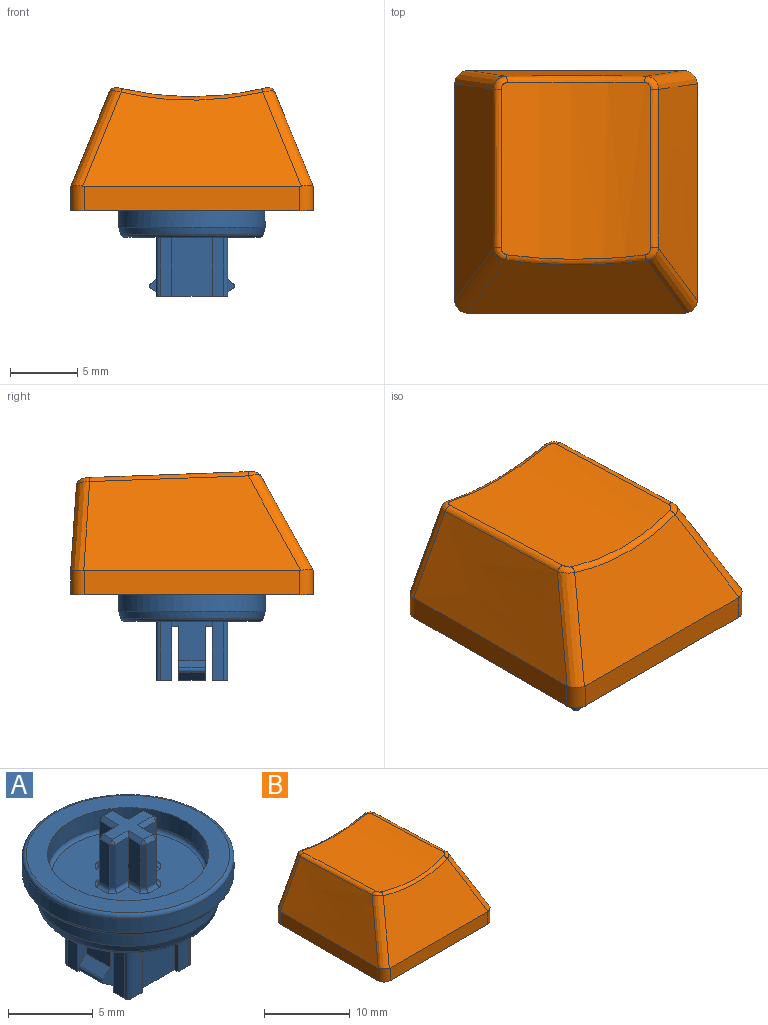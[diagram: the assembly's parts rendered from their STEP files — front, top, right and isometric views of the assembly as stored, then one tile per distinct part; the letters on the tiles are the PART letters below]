
ASSEMBLY  parts=2 mates=1
PART A: 171 faces, bbox 13.5x13.5x10 mm
  f0: cylinder r=4.2mm len=8.4mm, axis (0,0,-1), area 2.6mm2, adj f169,f170
  f1: plane 10.05x10.05mm, normal (0,0,-1), area 17.1mm2, adj f4,f170
  f2: cone r=5.25mm half-angle=15.9deg, axis (0,0,1), area 17mm2, adj f3,f4
  f3: cylinder r=5.45mm len=10.9mm, axis (0,0,-1), area 44.5mm2, adj f2,f79
  f4: torus R=5.02mm, axis (0,0,1), area 12.6mm2, adj f1,f2
  f5: plane 0.9x0.9mm, normal (0,0,-1), area 0.6mm2, adj f14
  f6: plane 0.5x0.2mm, normal (0,-0.71,-0.71), area 0.1mm2, adj f11,f15,f16,f17
  f7: plane 0.5x0.2mm, normal (-0.71,0,-0.71), area 0.1mm2, adj f10,f18,f19,f20
  f8: plane 0.5x0.2mm, normal (0,0.71,-0.71), area 0.1mm2, adj f13,f21,f22,f23
  f9: plane 0.5x0.2mm, normal (0.71,0,-0.71), area 0.1mm2, adj f12,f24,f25,f26
  f10: plane 0.5x0.09mm, normal (0,0,-1), area 0mm2, adj f7,f18,f20,f27
  f11: plane 0.5x0.09mm, normal (0,0,-1), area 0mm2, adj f6,f15,f17,f27
  f12: plane 0.5x0.09mm, normal (0,0,-1), area 0mm2, adj f9,f24,f26,f27
  f13: plane 0.5x0.09mm, normal (0,0,-1), area 0mm2, adj f8,f21,f23,f27
  f14: torus R=0.45mm, axis (0,0,-1), area 1.9mm2, adj f5,f27
  f15: plane 2.5x0.29mm, normal (1,0,0), area 0.7mm2, adj f6,f11,f16,f27,f34
  f16: plane 2.3x0.5mm, normal (0,-1,0), area 1.1mm2, adj f6,f15,f17,f34
  f17: plane 2.5x0.29mm, normal (-1,0,0), area 0.7mm2, adj f6,f11,f16,f27,f34
  f18: plane 2.5x0.29mm, normal (0,-1,0), area 0.7mm2, adj f7,f10,f19,f27,f34
  f19: plane 2.3x0.5mm, normal (-1,0,0), area 1.1mm2, adj f7,f18,f20,f34
  f20: plane 2.5x0.29mm, normal (0,1,0), area 0.7mm2, adj f7,f10,f19,f27,f34
  f21: plane 2.5x0.29mm, normal (-1,0,0), area 0.7mm2, adj f8,f13,f22,f27,f34
  f22: plane 2.3x0.5mm, normal (0,1,0), area 1.1mm2, adj f8,f21,f23,f34
  f23: plane 2.5x0.29mm, normal (1,0,0), area 0.7mm2, adj f8,f13,f22,f27,f34
  f24: plane 2.5x0.29mm, normal (0,1,0), area 0.7mm2, adj f9,f12,f25,f27,f34
  f25: plane 2.3x0.5mm, normal (1,0,0), area 1.1mm2, adj f9,f24,f26,f34
  f26: plane 2.5x0.29mm, normal (0,-1,0), area 0.7mm2, adj f9,f12,f25,f27,f34
  f27: cylinder r=0.75mm len=2.7mm, axis (0,0,1), area 7.6mm2, adj f10,f11,f12,f13,f14,f15,f17,f18
  f28: plane 2x0.91mm, normal (0.55,0,-0.83), area 2.2mm2, adj f29,f33,f35,f37
  f29: cylinder r=0.2mm len=2mm, axis (0,1,0), area 0.7mm2, adj f28,f35,f37,f38
  f30: plane 2x0.91mm, normal (-0.55,0,-0.83), area 2.2mm2, adj f31,f32,f40,f41
  f31: cylinder r=0.2mm len=2mm, axis (0,1,0), area 0.7mm2, adj f30,f40,f41,f42
  f32: plane 2x0.3mm, normal (0,0,-1), area 0.6mm2, adj f30,f40,f41,f46
  f33: plane 2x0.3mm, normal (0,0,-1), area 0.6mm2, adj f28,f35,f37,f48
  f34: plane 3.75x3.75mm, normal (0,0,-1), area 11.8mm2, adj f15,f16,f17,f18,f19,f20,f21,f22
  f35: plane 4x1.3mm, normal (0,-1,0), area 2.9mm2, adj f28,f29,f33,f38,f39,f48,f50
  f36: plane 0.6x0.5mm, normal (0,0,-1), area 0.3mm2, adj f37,f48,f49,f50
  f37: plane 4x1.3mm, normal (0,1,0), area 2.9mm2, adj f28,f29,f33,f36,f38,f48,f50
  f38: plane 2x0.63mm, normal (0.64,0,0.77), area 1.6mm2, adj f29,f35,f37,f50
  f39: plane 0.6x0.5mm, normal (0,0,-1), area 0.3mm2, adj f35,f48,f50,f51
  f40: plane 4x1.3mm, normal (0,1,0), area 2.9mm2, adj f30,f31,f32,f42,f43,f46,f59
  f41: plane 4x1.3mm, normal (0,-1,0), area 2.9mm2, adj f30,f31,f32,f42,f44,f46,f59
  f42: plane 2x0.63mm, normal (-0.64,0,0.77), area 1.6mm2, adj f31,f40,f41,f59
  f43: plane 0.6x0.5mm, normal (0,0,-1), area 0.3mm2, adj f40,f46,f59,f67
  f44: plane 0.6x0.5mm, normal (0,0,-1), area 0.3mm2, adj f41,f46,f59,f68
  f45: plane 5x3.75mm, normal (0,1,0), area 18.8mm2, adj f34,f46,f48,f72
  f46: plane 5x3.75mm, normal (1,0,0), area 14.8mm2, adj f32,f34,f40,f41,f43,f44,f45,f47
  f47: plane 5x3.75mm, normal (0,-1,0), area 18.8mm2, adj f34,f46,f48,f63
  f48: plane 5x3.75mm, normal (-1,0,0), area 14.8mm2, adj f33,f34,f35,f36,f37,f39,f45,f47
  f49: plane 4.75x0.8mm, normal (0,-1,0), area 3.3mm2, adj f36,f48,f50,f63,f66,f147
  f50: plane 3.3x3mm, normal (1,0,0), area 7.4mm2, adj f35,f36,f37,f38,f39,f49,f51,f149
  f51: plane 4.75x0.8mm, normal (0,1,0), area 3.3mm2, adj f39,f48,f50,f71,f72,f151
  f52: plane 4.75x3mm, normal (0,1,0), area 14.2mm2, adj f53,f54,f63,f152
  f53: plane 4.75x0.3mm, normal (1,0,0), area 1.4mm2, adj f52,f62,f63,f154
  f54: plane 4.75x0.3mm, normal (-1,0,0), area 1.4mm2, adj f52,f63,f65,f150
  f55: plane 4.75x3mm, normal (0,-1,0), area 14.2mm2, adj f56,f58,f72,f161
  f56: plane 4.75x0.3mm, normal (1,0,0), area 1.4mm2, adj f55,f72,f75,f163
  f57: plane 7.9x7.9mm, normal (0,0,-1), area 17.6mm2, adj f145,f146,f147,f148,f149,f150,f151,f152
  f58: plane 4.75x0.3mm, normal (-1,0,0), area 1.4mm2, adj f55,f70,f72,f159
  f59: plane 3.3x3mm, normal (-1,0,0), area 7.4mm2, adj f40,f41,f42,f43,f44,f67,f68,f164
  f60: cylinder r=0.3mm len=4.75mm, axis (0,0,-1), area 2.2mm2, adj f61,f62,f63,f158
  f61: plane 4.75x0.88mm, normal (-1,0,0), area 4.2mm2, adj f60,f63,f67,f160
  f62: plane 4.75x0.88mm, normal (0,1,0), area 4.2mm2, adj f53,f60,f63,f156
  f63: plane 5.35x1.18mm, normal (0,0,-1), area 3.9mm2, adj f46,f47,f48,f49,f52,f53,f54,f60
  f64: cylinder r=0.3mm len=4.75mm, axis (0,0,1), area 2.2mm2, adj f63,f65,f66,f146
  f65: plane 4.75x0.88mm, normal (0,1,0), area 4.2mm2, adj f54,f63,f64,f148
  f66: plane 4.75x0.88mm, normal (1,0,0), area 4.2mm2, adj f49,f63,f64,f145
  f67: plane 4.75x0.8mm, normal (0,-1,0), area 3.4mm2, adj f43,f46,f59,f61,f63,f162
  f68: plane 4.75x0.8mm, normal (0,1,0), area 3.4mm2, adj f44,f46,f59,f72,f74,f166
  f69: cylinder r=0.3mm len=4.75mm, axis (0,0,-1), area 2.2mm2, adj f70,f71,f72,f155
  f70: plane 4.75x0.88mm, normal (0,-1,0), area 4.2mm2, adj f58,f69,f72,f157
  f71: plane 4.75x0.88mm, normal (1,0,0), area 4.2mm2, adj f51,f69,f72,f153
  f72: plane 5.35x1.18mm, normal (0,0,-1), area 3.9mm2, adj f45,f46,f48,f51,f55,f56,f58,f68
  f73: cylinder r=0.3mm len=4.75mm, axis (0,0,1), area 2.2mm2, adj f72,f74,f75,f167
  f74: plane 4.75x0.88mm, normal (-1,0,0), area 4.2mm2, adj f68,f72,f73,f168
  f75: plane 4.75x0.88mm, normal (0,-1,0), area 4.2mm2, adj f56,f72,f73,f165
  f76: cylinder r=6.25mm len=12.5mm, axis (0,0,-1), area 39.3mm2, adj f143,f144
  f77: cylinder r=4.75mm len=9.5mm, axis (0,0,-1), area 37.3mm2, adj f78,f142
  f78: plane 12x12mm, normal (0,0,1), area 42.2mm2, adj f77,f144
  f79: plane 12x12mm, normal (0,0,-1), area 19.8mm2, adj f3,f143
  f80: plane 9x9mm, normal (0,0,1), area 51.8mm2, adj f122,f123,f124,f125,f126,f127,f128,f129
  f81: plane 3.1x1.06mm, normal (1,0,0), area 3.3mm2, adj f92,f118,f121,f127
  f82: plane 3.1x0.78mm, normal (0,1,0), area 2.4mm2, adj f115,f119,f121,f123
  f83: plane 3.1x1.06mm, normal (-1,0,0), area 3.3mm2, adj f84,f114,f115,f124
  f84: plane 3.1x1.06mm, normal (0,1,0), area 3.3mm2, adj f83,f107,f112,f126
  f85: plane 3.1x0.78mm, normal (-1,0,0), area 2.4mm2, adj f101,f106,f107,f130
  f86: plane 3.1x1.06mm, normal (0,-1,0), area 3.3mm2, adj f87,f100,f101,f134
  f87: plane 3.1x1.06mm, normal (-1,0,0), area 3.3mm2, adj f86,f94,f98,f136
  f88: plane 3.1x0.78mm, normal (0,-1,0), area 2.4mm2, adj f94,f96,f97,f140
  f89: plane 3.1x1.06mm, normal (1,0,0), area 3.3mm2, adj f90,f96,f102,f139
  f90: plane 3.1x1.06mm, normal (0,-1,0), area 3.3mm2, adj f89,f104,f105,f137
  f91: plane 3.1x0.78mm, normal (1,0,0), area 2.4mm2, adj f104,f110,f111,f133
  f92: plane 3.1x1.06mm, normal (0,1,0), area 3.3mm2, adj f81,f110,f116,f129
  f93: plane 3.4x3.4mm, normal (0,0,1), area 4.7mm2, adj f97,f98,f100,f102,f105,f106,f111,f112
  f94: plane 3.1x0.25mm, normal (-0.71,-0.71,0), area 1.1mm2, adj f87,f88,f95,f138
  f95: plane 0.25x0.25mm, normal (-0.58,-0.58,0.58), area 0.1mm2, adj f94,f97,f98
  f96: plane 3.1x0.25mm, normal (0.71,-0.71,0), area 1.1mm2, adj f88,f89,f99,f141
  f97: plane 0.78x0.25mm, normal (0,-0.71,0.71), area 0.3mm2, adj f88,f93,f95,f99
  f98: plane 1.31x0.25mm, normal (-0.71,0,0.71), area 0.4mm2, adj f87,f93,f95,f100
  f99: plane 0.25x0.25mm, normal (0.58,-0.58,0.58), area 0.1mm2, adj f96,f97,f102
  f100: plane 1.31x0.25mm, normal (0,-0.71,0.71), area 0.4mm2, adj f86,f93,f98,f103
  f101: plane 3.1x0.25mm, normal (-0.71,-0.71,0), area 1.1mm2, adj f85,f86,f103,f132
  f102: plane 1.31x0.25mm, normal (0.71,0,0.71), area 0.4mm2, adj f89,f93,f99,f105
  f103: plane 0.25x0.25mm, normal (-0.58,-0.58,0.58), area 0.1mm2, adj f100,f101,f106
  f104: plane 3.1x0.25mm, normal (0.71,-0.71,0), area 1.1mm2, adj f90,f91,f108,f135
  f105: plane 1.31x0.25mm, normal (0,-0.71,0.71), area 0.4mm2, adj f90,f93,f102,f108
  f106: plane 0.78x0.25mm, normal (-0.71,0,0.71), area 0.3mm2, adj f85,f93,f103,f109
  f107: plane 3.1x0.25mm, normal (-0.71,0.71,0), area 1.1mm2, adj f84,f85,f109,f128
  f108: plane 0.25x0.25mm, normal (0.58,-0.58,0.58), area 0.1mm2, adj f104,f105,f111
  f109: plane 0.25x0.25mm, normal (-0.58,0.58,0.58), area 0.1mm2, adj f106,f107,f112
  f110: plane 3.1x0.25mm, normal (0.71,0.71,0), area 1.1mm2, adj f91,f92,f113,f131
  f111: plane 0.78x0.25mm, normal (0.71,0,0.71), area 0.3mm2, adj f91,f93,f108,f113
  f112: plane 1.31x0.25mm, normal (0,0.71,0.71), area 0.4mm2, adj f84,f93,f109,f114
  f113: plane 0.25x0.25mm, normal (0.58,0.58,0.58), area 0.1mm2, adj f110,f111,f116
  f114: plane 1.31x0.25mm, normal (-0.71,0,0.71), area 0.4mm2, adj f83,f93,f112,f117
  f115: plane 3.1x0.25mm, normal (-0.71,0.71,0), area 1.1mm2, adj f82,f83,f117,f122
  f116: plane 1.31x0.25mm, normal (0,0.71,0.71), area 0.4mm2, adj f92,f93,f113,f118
  f117: plane 0.25x0.25mm, normal (-0.58,0.58,0.58), area 0.1mm2, adj f114,f115,f119
  f118: plane 1.31x0.25mm, normal (0.71,0,0.71), area 0.4mm2, adj f81,f93,f116,f120
  f119: plane 0.78x0.25mm, normal (0,0.71,0.71), area 0.3mm2, adj f82,f93,f117,f120
  f120: plane 0.25x0.25mm, normal (0.58,0.58,0.58), area 0.1mm2, adj f118,f119,f121
  f121: plane 3.1x0.25mm, normal (0.71,0.71,0), area 1.1mm2, adj f81,f82,f120,f125
  f122: cylinder r=0.25mm len=0.57mm, axis (0.71,0.71,0), area 0.2mm2, adj f80,f115,f123,f124
  f123: cylinder r=0.25mm len=0.99mm, axis (-1,0,0), area 0.3mm2, adj f80,f82,f122,f125
  f124: cylinder r=0.25mm len=1.16mm, axis (0,-1,0), area 0.4mm2, adj f80,f83,f122,f126
  f125: cylinder r=0.25mm len=0.57mm, axis (-0.71,0.71,0), area 0.2mm2, adj f80,f121,f123,f127
  f126: cylinder r=0.25mm len=1.16mm, axis (-1,0,0), area 0.4mm2, adj f80,f84,f124,f128
  f127: cylinder r=0.25mm len=1.16mm, axis (0,1,0), area 0.4mm2, adj f80,f81,f125,f129
  f128: cylinder r=0.25mm len=0.57mm, axis (0.71,0.71,0), area 0.2mm2, adj f80,f107,f126,f130
  f129: cylinder r=0.25mm len=1.16mm, axis (-1,0,0), area 0.4mm2, adj f80,f92,f127,f131
  f130: cylinder r=0.25mm len=0.99mm, axis (0,-1,0), area 0.3mm2, adj f80,f85,f128,f132
  f131: cylinder r=0.25mm len=0.57mm, axis (-0.71,0.71,0), area 0.2mm2, adj f80,f110,f129,f133
  f132: cylinder r=0.25mm len=0.57mm, axis (0.71,-0.71,0), area 0.2mm2, adj f80,f101,f130,f134
  f133: cylinder r=0.25mm len=0.99mm, axis (0,1,0), area 0.3mm2, adj f80,f91,f131,f135
  f134: cylinder r=0.25mm len=1.16mm, axis (1,0,0), area 0.4mm2, adj f80,f86,f132,f136
  f135: cylinder r=0.25mm len=0.57mm, axis (-0.71,-0.71,0), area 0.2mm2, adj f80,f104,f133,f137
  f136: cylinder r=0.25mm len=1.16mm, axis (0,-1,0), area 0.4mm2, adj f80,f87,f134,f138
  f137: cylinder r=0.25mm len=1.16mm, axis (1,0,0), area 0.4mm2, adj f80,f90,f135,f139
  f138: cylinder r=0.25mm len=0.57mm, axis (0.71,-0.71,0), area 0.2mm2, adj f80,f94,f136,f140
  f139: cylinder r=0.25mm len=1.16mm, axis (0,1,0), area 0.4mm2, adj f80,f89,f137,f141
  f140: cylinder r=0.25mm len=0.99mm, axis (1,0,0), area 0.3mm2, adj f80,f88,f138,f141
  f141: cylinder r=0.25mm len=0.57mm, axis (-0.71,-0.71,0), area 0.2mm2, adj f80,f96,f139,f140
  f142: torus R=4.5mm, axis (0,0,1), area 11.5mm2, adj f77,f80
  f143: torus R=6mm, axis (0,0,1), area 15.2mm2, adj f76,f79
  f144: torus R=6mm, axis (0,0,1), area 15.2mm2, adj f76,f78
  f145: cylinder r=0.25mm len=1.13mm, axis (0,1,0), area 0.4mm2, adj f57,f66,f146,f147
  f146: torus R=0.55mm, axis (0,0,-1), area 0.2mm2, adj f57,f64,f145,f148
  f147: cylinder r=0.25mm len=0.45mm, axis (1,0,0), area 0.1mm2, adj f49,f57,f145,f149
  f148: cylinder r=0.25mm len=1.13mm, axis (-1,0,0), area 0.4mm2, adj f57,f65,f146,f150
  f149: cylinder r=0.25mm len=3mm, axis (0,1,0), area 1.1mm2, adj f50,f57,f147,f151
  f150: cylinder r=0.25mm len=0.55mm, axis (0,-1,0), area 0.1mm2, adj f54,f57,f148,f152
  f151: cylinder r=0.25mm len=0.45mm, axis (-1,0,0), area 0.1mm2, adj f51,f57,f149,f153
  f152: cylinder r=0.25mm len=3mm, axis (-1,0,0), area 1.1mm2, adj f52,f57,f150,f154
  f153: cylinder r=0.25mm len=1.13mm, axis (0,1,0), area 0.4mm2, adj f57,f71,f151,f155
  f154: cylinder r=0.25mm len=0.55mm, axis (0,1,0), area 0.1mm2, adj f53,f57,f152,f156
  f155: torus R=0.55mm, axis (0,0,-1), area 0.2mm2, adj f57,f69,f153,f157
  f156: cylinder r=0.25mm len=1.13mm, axis (-1,0,0), area 0.4mm2, adj f57,f62,f154,f158
  f157: cylinder r=0.25mm len=1.13mm, axis (1,0,0), area 0.4mm2, adj f57,f70,f155,f159
  f158: torus R=0.55mm, axis (0,0,-1), area 0.2mm2, adj f57,f60,f156,f160
  f159: cylinder r=0.25mm len=0.55mm, axis (0,-1,0), area 0.1mm2, adj f57,f58,f157,f161
  f160: cylinder r=0.25mm len=1.13mm, axis (0,-1,0), area 0.4mm2, adj f57,f61,f158,f162
  f161: cylinder r=0.25mm len=3mm, axis (1,0,0), area 1.1mm2, adj f55,f57,f159,f163
  f162: cylinder r=0.25mm len=0.45mm, axis (1,0,0), area 0.1mm2, adj f57,f67,f160,f164
  f163: cylinder r=0.25mm len=0.55mm, axis (0,1,0), area 0.1mm2, adj f56,f57,f161,f165
  f164: cylinder r=0.25mm len=3mm, axis (0,-1,0), area 1.1mm2, adj f57,f59,f162,f166
  f165: cylinder r=0.25mm len=1.13mm, axis (1,0,0), area 0.4mm2, adj f57,f75,f163,f167
  f166: cylinder r=0.25mm len=0.45mm, axis (-1,0,0), area 0.1mm2, adj f57,f68,f164,f168
  f167: torus R=0.55mm, axis (0,0,-1), area 0.2mm2, adj f57,f73,f165,f168
  f168: cylinder r=0.25mm len=1.13mm, axis (0,-1,0), area 0.4mm2, adj f57,f74,f166,f167
  f169: torus R=3.95mm, axis (0,0,-1), area 10.1mm2, adj f0,f57
  f170: torus R=4.45mm, axis (0,0,1), area 10.6mm2, adj f0,f1
PART B: 50 faces, bbox 21.6x22.4x13.2 mm
  f0: plane 18.1x18.1mm, normal (0,0,-1), area 67.5mm2, adj f1,f2,f3,f4,f10,f12,f14,f16
  f1: plane 16.1x1.8mm, normal (1,0,0), area 29mm2, adj f0,f8,f10,f16
  f2: plane 16.11x1.81mm, normal (0,1,0), area 29mm2, adj f0,f5,f14,f15,f16,f17
  f3: plane 16.1x1.8mm, normal (-1,0,0), area 29mm2, adj f0,f6,f12,f14
  f4: plane 16.1x1.8mm, normal (0,-1,0), area 29mm2, adj f0,f7,f10,f12
  f5: plane 15.98x6.33mm, normal (0,1,0.07), area 79.8mm2, adj f2,f15,f17,f20
  f6: bspline ~18.1x7.49mm, area 104.4mm2, adj f3,f12,f13,f14,f15,f19
  f7: plane 16.33x7.03mm, normal (0,-0.87,0.48), area 103.3mm2, adj f4,f10,f11,f12,f13,f23
  f8: bspline ~18.1x7.49mm, area 104.4mm2, adj f1,f10,f11,f16,f17,f24
  f9: cylinder r=22.9mm len=12.87mm, axis (0,1,-0.04), area 144.5mm2, adj f18,f19,f20,f21,f22,f23,f24,f25
  f10: cylinder r=1mm len=1.88mm, axis (0,0,-1), area 2.9mm2, adj f0,f1,f4,f7,f8,f11
  f11: bspline ~9.11x5.74mm, area 11.9mm2, adj f7,f8,f10,f25
  f12: cylinder r=1mm len=1.88mm, axis (0,0,1), area 2.9mm2, adj f0,f3,f4,f6,f7,f13
  f13: bspline ~9.11x5.74mm, area 11.9mm2, adj f6,f7,f12,f21
  f14: cylinder r=1mm len=1.81mm, axis (0,0,-1), area 2.8mm2, adj f0,f2,f3,f6,f15
  f15: bspline ~11.15x5.6mm, area 11mm2, adj f2,f5,f6,f14,f18
  f16: cylinder r=1mm len=1.81mm, axis (0,0,1), area 2.8mm2, adj f0,f1,f2,f8,f17
  f17: bspline ~11.16x5.6mm, area 11mm2, adj f2,f5,f8,f16,f22
  f18: bspline ~1.21x1.09mm, area 0.9mm2, adj f9,f15,f19,f20
  f19: bspline ~17.91x1.05mm, area 8.4mm2, adj f6,f9,f18,f21
  f20: bspline ~10.48x1.05mm, area 7.6mm2, adj f5,f9,f18,f22
  f21: bspline ~1.23x1.13mm, area 0.7mm2, adj f9,f13,f19,f23
  f22: bspline ~1.25x1.04mm, area 0.9mm2, adj f9,f17,f20,f24
  f23: bspline ~10.58x0.84mm, area 5.8mm2, adj f7,f9,f21,f25
  f24: bspline ~17.91x1.05mm, area 8.4mm2, adj f8,f9,f22,f25
  f25: bspline ~1.23x1.02mm, area 0.7mm2, adj f9,f11,f23,f24
  f26: plane 16.11x1.61mm, normal (-1,0,0), area 25.7mm2, adj f0,f27,f29,f32,f33
  f27: plane 16.1x1.77mm, normal (0,-1,0), area 28.4mm2, adj f0,f26,f28,f30,f31,f33
  f28: plane 16.11x1.61mm, normal (1,0,0), area 25.7mm2, adj f0,f27,f29,f31,f32
  f29: plane 16.1x1.54mm, normal (0,1,0), area 24.8mm2, adj f0,f26,f28,f32
  f30: plane 16.08x6.01mm, normal (0,-1,-0.07), area 74.4mm2, adj f27,f31,f33,f34
  f31: offset ~20.1x9.49mm, area 95.9mm2, adj f27,f28,f30,f32,f34
  f32: plane 16.73x7.17mm, normal (0,0.87,-0.48), area 95.8mm2, adj f26,f28,f29,f31,f33,f34
  f33: offset ~20.1x9.49mm, area 95.9mm2, adj f26,f27,f30,f32,f34
  f34: cylinder r=23.9mm len=12.1mm, axis (0,1,-0.04), area 108.1mm2, adj f30,f31,f32,f33,f46
  f35: plane 7.29x1.35mm, normal (-1,0,0), area 9.8mm2, adj f36,f44,f45,f49
  f36: plane 7.37x1.5mm, normal (0,-1,0), area 11mm2, adj f35,f37,f45,f49
  f37: plane 7.41x1.3mm, normal (-1,0,0), area 9.6mm2, adj f36,f38,f45,f49
  f38: plane 7.41x1.5mm, normal (0,1,0), area 11mm2, adj f37,f39,f45,f49
  f39: plane 7.38x1.35mm, normal (-1,0,0), area 9.9mm2, adj f38,f40,f45,f49
  f40: plane 7.38x1mm, normal (0,1,0), area 7.4mm2, adj f39,f41,f45,f49
  f41: plane 7.38x1.35mm, normal (1,0,0), area 9.9mm2, adj f40,f42,f45,f49
  f42: plane 7.41x1.5mm, normal (0,1,0), area 11mm2, adj f41,f43,f45,f49
  f43: plane 7.41x1.3mm, normal (1,0,0), area 9.6mm2, adj f42,f45,f47,f49
  f44: plane 7.24x1mm, normal (0,-1,0), area 7.2mm2, adj f35,f45,f48,f49
  f45: plane 5.5x5.5mm, normal (0,0,-1), area 15.9mm2, adj f35,f36,f37,f38,f39,f40,f41,f42
  f46: cylinder r=2.75mm len=7.46mm, axis (0,0,-1), area 129mm2, adj f34,f45
  f47: plane 7.37x1.5mm, normal (0,-1,0), area 11mm2, adj f43,f45,f48,f49
  f48: plane 7.29x1.35mm, normal (1,0,0), area 9.8mm2, adj f44,f45,f47,f49
  f49: cylinder r=23.9mm len=4mm, axis (0,1,-0.04), area 7.9mm2, adj f35,f36,f37,f38,f39,f40,f41,f42
PLACE A at identity
PLACE B at identity fixed
MATE fastened B.f46 <-> A.f77  axis (0,0,-1) through (0,0,0)mm
